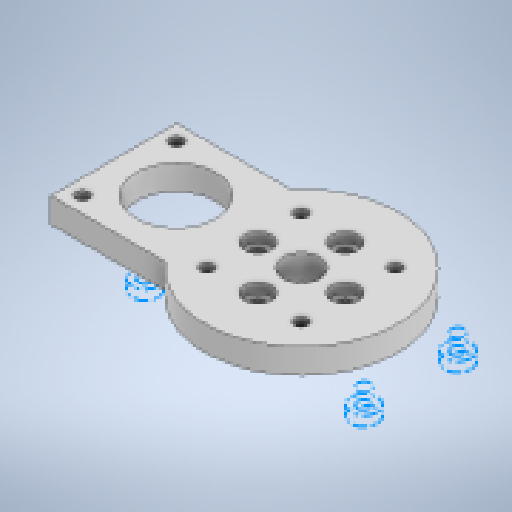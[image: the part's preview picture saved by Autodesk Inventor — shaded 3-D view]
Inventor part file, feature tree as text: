
AUTODESK INVENTOR PART (.ipt)
format: ipt  version: 2024 (Build 280153000, 153)  size: 309,760 bytes
history: native  units: in
note: dims shown in document units (in); Inventor stores cm internally (conversion verified against a paired STEP export)
features: sketch x6, reference x6, extrude x4, other x4, hole x2
ambient origin geometry x8: Origin, YZ Plane, XZ Plane, XY Plane, X Axis, Y Axis, Z Axis, Center Point
bodies: Solid1 (feature_tree)
feature tree (22):
  extrude  "Extrusion1"  Depth=0.7929in
  extrude  "Extrusion2"  Depth=0.1575in
  extrude  "Extrusion4"  Depth=1.2205in
  hole  "Hole4"  [1 undecoded]
  extrude  "Extrusion5"  [1 undecoded]
  hole  "Hole5"  [1 undecoded]
  sketch  "Sketch1"  dims[d0=1.5787in d1=0.7929in]
  sketch  "Sketch3"  dims[d2=0.1575in d3=0.0in d11=0.5118in]
  reference  "Reference3"
  sketch  "Sketch7"  dims[d12=0.0in d13=0.0in d31=1.2205in]
  reference  "Reference9"
  sketch  "Sketch8"  dims[d32=0.3937in d33=0.0in]
  reference  "Reference10"
  sketch  "Sketch9"  dims[d34=0.0827in d35=0.2362in d36=0.1693in d37=0.0591in d38=90.0deg d39=0.315in d40=0.8108in d41=0.2343in]
  reference  "Reference11"
  reference  "Reference12"
  sketch  "Sketch10"  dims[d42=0.0in d43=0.0in d44=0.0827in d45=0.2362in d46=0.1693in d47=0.0591in d48=90.0deg d49=0.315in d50=0.8108in]
  reference  "Reference13"
  other  "gripper_test.iam"
  other  "HTD-45H:1"
  other  "테프론:1"
  other  "Top Horn:2"
note: 3 required parameter values undecoded (feature->parameter linkage not recoverable at this tier; creation-order binding heuristic only, values carry confidence <= 0.55)
